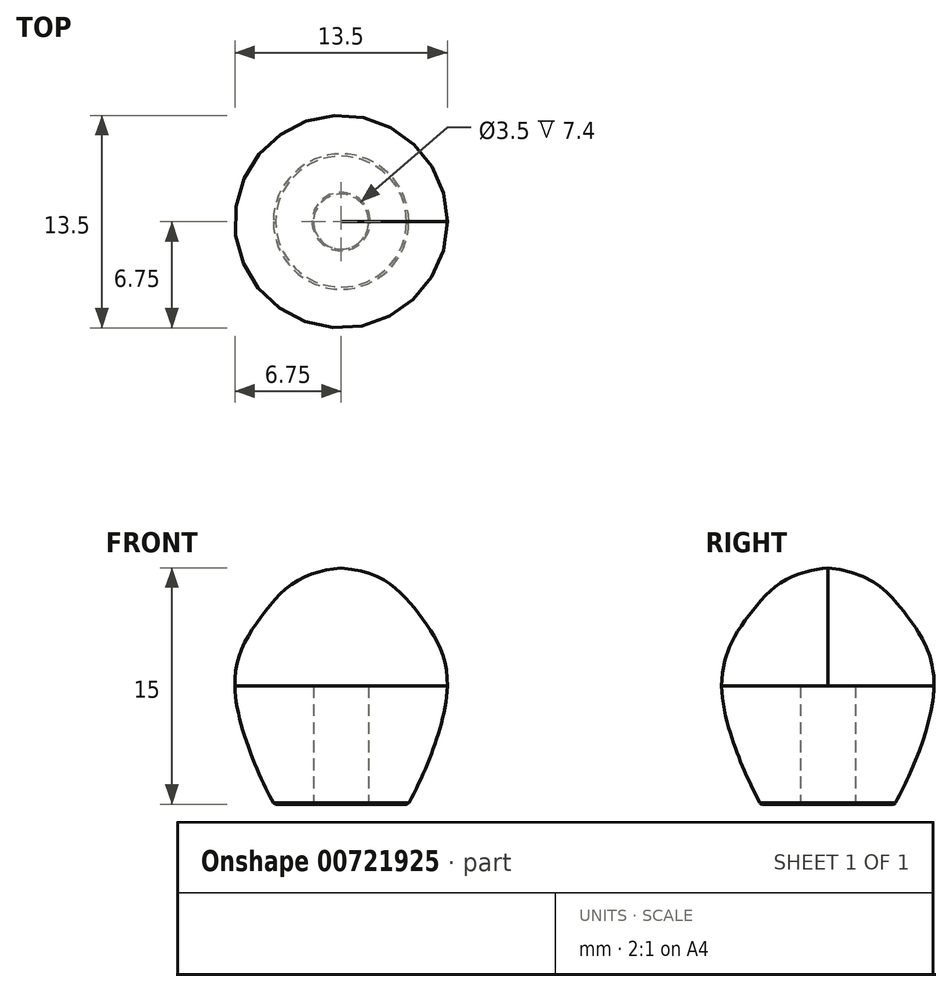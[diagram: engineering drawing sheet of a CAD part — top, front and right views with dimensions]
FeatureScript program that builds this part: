
annotation { "Feature Type Name" : "Feature", "Feature Type Description" : "" }
export const myFeature = defineFeature(function(context is Context, id is Id, definition is map)
    precondition{}
    {
        {
            var Q0;
            Q0=qCreatedBy(makeId("Front.planeOp"),FACE);
            var sketch = newSketch(context, id + "F0", { "sketchPlane" : qUnion([Q0])});
            skLineSegment(sketch, "E0", {"start": v(0, 0) * mm, "end": v(1.75, 0) * mm});
            skLineSegment(sketch, "E1", {"start": v(0, 0) * mm, "end": v(0, 7.5) * mm});
            skLineSegment(sketch, "E2", {"start": v(1.75, 0) * mm, "end": v(6.75, 0) * mm});
            skPoint(sketch, "E3.3.internal.snap0", {"position": v(4.25, 0) * mm});
            skFitSpline(sketch, "E3", {"points": [v(0, 7.5) * mm, v(4.86, 4.68) * mm, v(6.75, 0) * mm, v(4.25, -7.5) * mm], "startDerivative": vector(25.83, -2.27) * mm, "endDerivative": vector(-6.7, -11.81) * mm});
            skLineSegment(sketch, "E4", {"start": v(4.25, -7.5) * mm, "end": v(1.75, -7.5) * mm});
            skLineSegment(sketch, "E5", {"start": v(1.75, -7.5) * mm, "end": v(1.75, 0) * mm});
            skSolve(sketch);
        }
        {
            var Q0;
            Q0=makeQuery(id+"F0.imprint","IMPRINT",FACE,{"disambiguationData":[TD([[makeQuery(id+"F0.imprint","IMPRINT",EDGE,{"derivedFrom":sQuery(id+"F0.wireOp",EDGE,"E0")}),1.0]])]});
            var Q1;
            {var subQ0=sQuery(id+"F0.wireOp",EDGE,"E2");Q1=makeQuery(id+"F0.imprint","IMPRINT",FACE,{"disambiguationData":[TD([[makeQuery(id+"F0.imprint","IMPRINT",EDGE,{"derivedFrom":subQ0}),-1.0]])]});}
            var Q2;
            Q2=sQuery(id+"F0.wireOp",EDGE,"E1");
            revolve(context, id + "F1", {"surfaceOperationType" : NewSurfaceOperationType.NEW, "entities" : qUnion([Q0, Q1]), "axis" : qUnion([Q2]), "revolveType" : RevolveType.FULL});
        }
        {
            var Q0;
            Q0=makeQuery(id+"F1.opRevolve","SWEPT_FACE",FACE,{"disambiguationData":[OSD([sQuery(id+"F0.wireOp",EDGE,"E4")])]});
            chamfer(context, id + "F2", {"entities" : qUnion([Q0]), "width" : 0.1 * mm, "tangentPropagation" : true});
        }
    });
